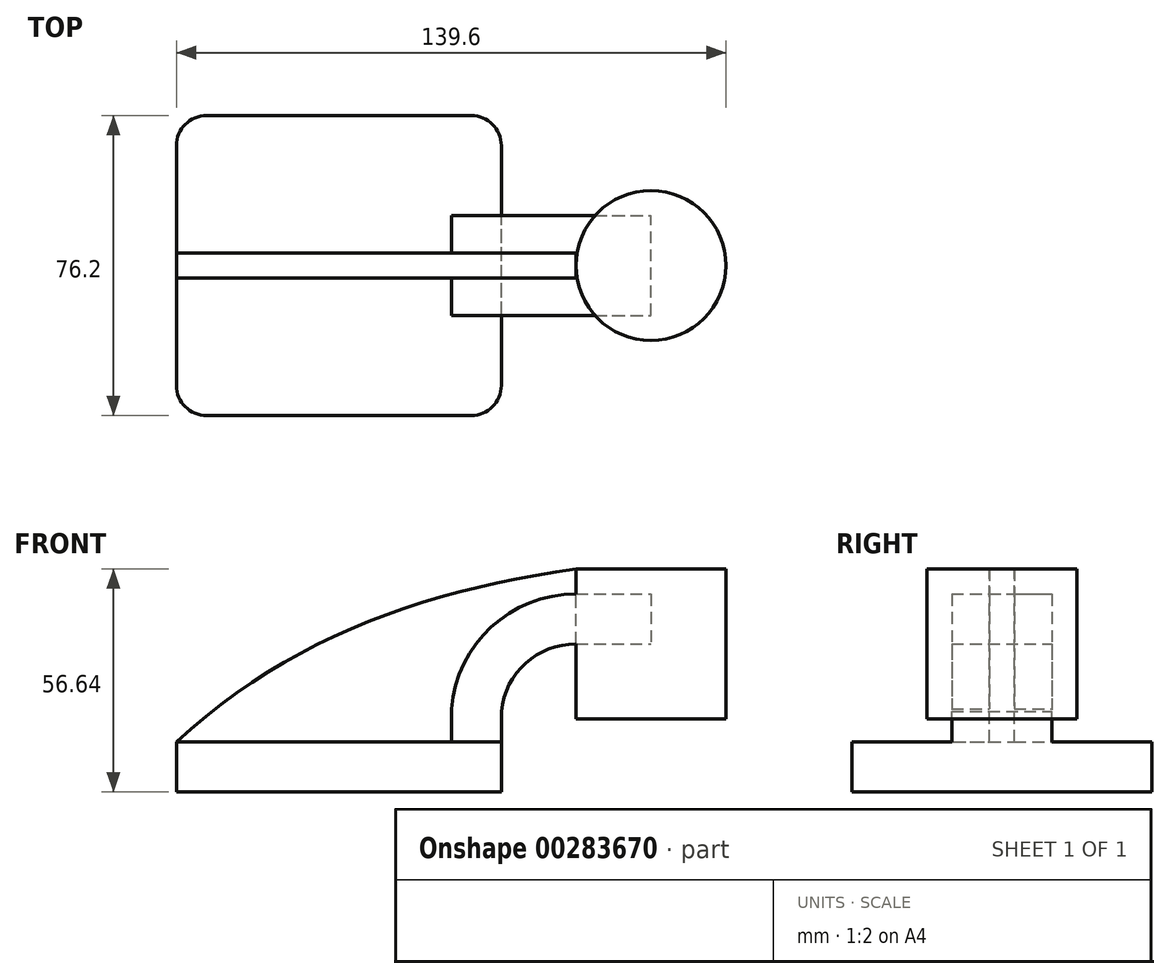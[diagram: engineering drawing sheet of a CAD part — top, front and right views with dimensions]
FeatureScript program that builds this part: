
annotation { "Feature Type Name" : "Feature", "Feature Type Description" : "" }
export const myFeature = defineFeature(function(context is Context, id is Id, definition is map)
    precondition{}
    {
        {
            var Q0;
            Q0=qCreatedBy(makeId("Front.planeOp"),FACE);
            var sketch = newSketch(context, id + "F0", { "sketchPlane" : qUnion([Q0])});
            skLineSegment(sketch, "E0.bottom", {"start": v(-41.28, 6.35) * mm, "end": v(41.27, 6.35) * mm});
            skLineSegment(sketch, "E0.top", {"start": v(-41.27, -6.35) * mm, "end": v(41.28, -6.35) * mm});
            skLineSegment(sketch, "E0.left", {"start": v(-41.28, 6.35) * mm, "end": v(-41.27, -6.35) * mm});
            skLineSegment(sketch, "E0.right", {"start": v(41.28, 6.35) * mm, "end": v(41.28, -6.35) * mm});
            skPoint(sketch, "E0.middle", {"position": v(0, 0) * mm});
            skLineSegment(sketch, "E1.bottom", {"start": v(60.22, 50.29) * mm, "end": v(98.32, 50.29) * mm});
            skLineSegment(sketch, "E1.top", {"start": v(60.22, 12.19) * mm, "end": v(98.32, 12.19) * mm});
            skLineSegment(sketch, "E1.left", {"start": v(60.22, 50.29) * mm, "end": v(60.22, 12.19) * mm});
            skLineSegment(sketch, "E1.right", {"start": v(98.32, 50.29) * mm, "end": v(98.32, 12.19) * mm});
            skPoint(sketch, "E1.middle", {"position": v(79.27, 31.24) * mm});
            skLineSegment(sketch, "E2", {"start": v(41.27, 6.35) * mm, "end": v(41.27, 14.14) * mm});
            skArc(sketch, "E3", {"start": v(60.22, 31.24) * mm, "mid": v(47.46, 26.33) * mm, "end": v(41.27, 14.14) * mm});
            skLineSegment(sketch, "E4", {"start": v(60.22, 31.24) * mm, "end": v(79.27, 31.24) * mm});
            skLineSegment(sketch, "E5.0", {"start": v(60.22, 43.94) * mm, "end": v(82.7, 43.94) * mm});
            skArc(sketch, "E5.1", {"start": v(60.22, 43.94) * mm, "mid": v(38.68, 35.51) * mm, "end": v(28.57, 14.7) * mm});
            skLineSegment(sketch, "E5.2", {"start": v(28.57, 6.35) * mm, "end": v(28.57, 14.7) * mm});
            skFitSpline(sketch, "E6", {"points": [v(-41.28, 6.35) * mm, v(60.22, 50.29) * mm], "startDerivative": vector(84.5, 78.28) * mm, "endDerivative": vector(117.85, 16.69) * mm});
            skLineSegment(sketch, "E7", {"start": v(79.27, 50.29) * mm, "end": v(79.27, 12.19) * mm});
            skSolve(sketch);
        }
        {
            var Q0;
            Q0=makeQuery(id+"F0.imprint","IMPRINT",FACE,{"disambiguationData":[TD([[makeQuery(id+"F0.imprint","IMPRINT",EDGE,{"derivedFrom":sQuery(id+"F0.wireOp",EDGE,"E0.top")}),1.0]])]});
            extrude(context, id + "F1", {"entities" : qUnion([Q0]), "endBound" : BoundingType.SYMMETRIC, "depth" : 76.2 * mm});
        }
        {
            var Q0;
            {var subQ1=sQuery(id+"F0.wireOp",EDGE,"E2");Q0=makeQuery(id+"F0.imprint","IMPRINT",FACE,{"disambiguationData":[TD([[makeQuery(id+"F0.imprint","IMPRINT",EDGE,{"derivedFrom":subQ1}),1.0]])]});}
            var Q1;
            {var subQ0=sQuery(id+"F0.wireOp",EDGE,"E4");Q1=makeQuery(id+"F0.imprint","IMPRINT",FACE,{"disambiguationData":[TD([[makeQuery(id+"F0.imprint","IMPRINT",EDGE,{"derivedFrom":subQ0}),1.0]])]});}
            extrude(context, id + "F2", {"entities" : qUnion([Q0, Q1]), "operationType" : NewBodyOperationType.ADD, "endBound" : BoundingType.SYMMETRIC, "depth" : 25.4 * mm});
        }
        {
            var Q0;
            {var subQ1=sQuery(id+"F0.wireOp",EDGE,"E5.1");Q0=makeQuery(id+"F0.imprint","IMPRINT",FACE,{"disambiguationData":[TD([[makeQuery(id+"F0.imprint","IMPRINT",EDGE,{"derivedFrom":subQ1}),-1.0]])]});}
            extrude(context, id + "F3", {"entities" : qUnion([Q0]), "operationType" : NewBodyOperationType.ADD, "endBound" : BoundingType.SYMMETRIC, "depth" : 6.35 * mm});
        }
        {
            var Q0;
            {var subQ4=sQuery(id+"F0.wireOp",EDGE,"E1.right");Q0=makeQuery(id+"F0.imprint","IMPRINT",FACE,{"disambiguationData":[TD([[makeQuery(id+"F0.imprint","IMPRINT",EDGE,{"derivedFrom":subQ4}),-1.0]])]});}
            var Q1;
            Q1=sQuery(id+"F0.wireOp",EDGE,"E7");
            revolve(context, id + "F4", {"entities" : qUnion([Q0]), "axis" : qUnion([Q1]), "revolveType" : RevolveType.FULL});
        }
        {
            var Q0;
            Q0=makeQuery(id+"F1.opExtrude","CAP_EDGE",EDGE,{"disambiguationData":[OSD([sQuery(id+"F0.wireOp",EDGE,"E0.right")])],"isStart":false});
            fillet(context, id + "F5", {"entities" : qUnion([Q0]), "radius" : 7.62 * mm, "tangentPropagation" : true, "allowEdgeOverflow" : false});
        }
        {
            var Q0;
            Q0=makeQuery(id+"F1.opExtrude","CAP_EDGE",EDGE,{"disambiguationData":[OSD([sQuery(id+"F0.wireOp",EDGE,"E0.right")])],"isStart":true});
            fillet(context, id + "F6", {"entities" : qUnion([Q0]), "radius" : 7.62 * mm, "tangentPropagation" : true, "allowEdgeOverflow" : false});
        }
        {
            var Q0;
            Q0=makeQuery(id+"F1.opExtrude","CAP_EDGE",EDGE,{"disambiguationData":[OSD([sQuery(id+"F0.wireOp",EDGE,"E0.left")])],"isStart":true});
            fillet(context, id + "F7", {"entities" : qUnion([Q0]), "radius" : 7.62 * mm, "tangentPropagation" : true, "allowEdgeOverflow" : false});
        }
        {
            var Q0;
            Q0=makeQuery(id+"F1.opExtrude","CAP_EDGE",EDGE,{"disambiguationData":[OSD([sQuery(id+"F0.wireOp",EDGE,"E0.left")])],"isStart":false});
            fillet(context, id + "F8", {"entities" : qUnion([Q0]), "radius" : 7.62 * mm, "tangentPropagation" : true, "allowEdgeOverflow" : false});
        }
    });
